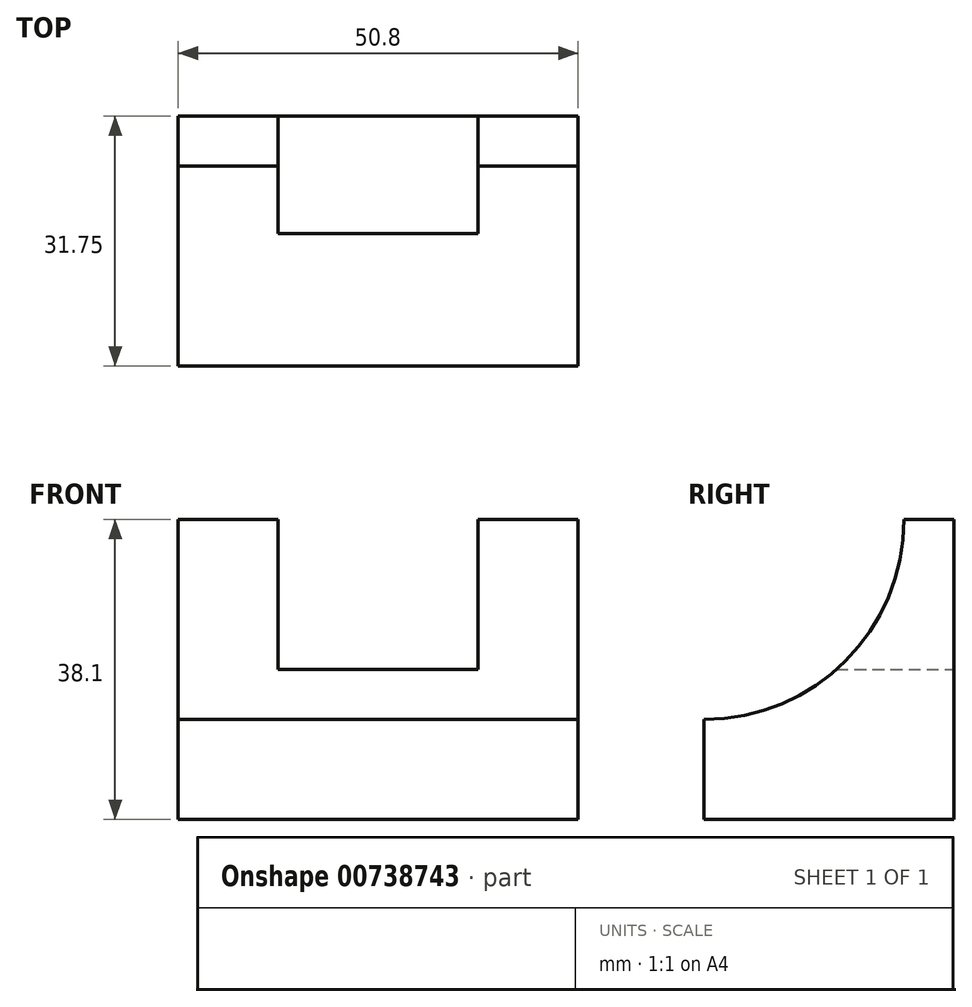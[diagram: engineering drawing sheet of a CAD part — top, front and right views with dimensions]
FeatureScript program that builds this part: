
annotation { "Feature Type Name" : "Feature", "Feature Type Description" : "" }
export const myFeature = defineFeature(function(context is Context, id is Id, definition is map)
    precondition{}
    {
        {
            var Q0;
            Q0=qCreatedBy(makeId("Right.planeOp"),FACE);
            var sketch = newSketch(context, id + "F0", { "sketchPlane" : qUnion([Q0])});
            skLineSegment(sketch, "E0", {"start": v(0, 0) * mm, "end": v(31.75, 0) * mm});
            skLineSegment(sketch, "E1", {"start": v(31.75, 0) * mm, "end": v(31.75, 38.1) * mm});
            skLineSegment(sketch, "E2", {"start": v(31.75, 38.1) * mm, "end": v(0, 38.1) * mm});
            skLineSegment(sketch, "E3", {"start": v(0, 38.1) * mm, "end": v(0, 0) * mm});
            skSolve(sketch);
        }
        {
            var Q0;
            Q0 = qSketchRegion(id + "F0", true);
            extrude(context, id + "F1", {"entities" : qUnion([Q0]), "depth" : 50.8 * mm, "offsetDistance" : 25.4 * mm});
        }
        {
            var Q0;
            Q0=makeQuery(id+"F1.opExtrude","CAP_FACE",FACE,{"disambiguationData":[OSD([sQuery(id+"F0.wireOp",EDGE,"E0"),sQuery(id+"F0.wireOp",EDGE,"E1"),sQuery(id+"F0.wireOp",EDGE,"E2"),sQuery(id+"F0.wireOp",EDGE,"E3")])],"isStart":true});
            var sketch = newSketch(context, id + "F2", { "sketchPlane" : qUnion([Q0])});
            skLineSegment(sketch, "E4", {"start": v(-31.75, 38.1) * mm, "end": v(-25.4, 38.1) * mm});
            skLineSegment(sketch, "E5", {"start": v(0, 0) * mm, "end": v(0, 12.7) * mm});
            skCircle(sketch, "E6", {"center": v(0, 38.1) * mm, "radius": 25.4 * mm});
            skSolve(sketch);
        }
        {
            var Q0;
            {var subQ1=makeQuery(id+"F1.opExtrude","CAP_EDGE",EDGE,{"disambiguationData":[OSD([sQuery(id+"F0.wireOp",EDGE,"E2")])],"isStart":true});var subQ3=makeQuery(id+"F1.opExtrude","CAP_EDGE",EDGE,{"disambiguationData":[OSD([sQuery(id+"F0.wireOp",EDGE,"E3")])],"isStart":true});var subQ5=makeQuery(id+"F2.imprint","INTERSECT",VERTEX,{"derivedFrom":[subQ1,subQ3]});Q0=makeQuery(id+"F2.imprint","IMPRINT",FACE,{"disambiguationData":[TD([[makeQuery(id+"F2.imprint","IMPRINT",EDGE,{"disambiguationData":[TD([[subQ5,1.0]])],"derivedFrom":subQ1}),-1.0]])]});}
            extrude(context, id + "F3", {"entities" : qUnion([Q0]), "operationType" : NewBodyOperationType.REMOVE, "endBound" : BoundingType.THROUGH_ALL, "oppositeDirection" : true, "depth" : 25.4 * mm, "offsetDistance" : 25.4 * mm});
        }
        {
            var Q0;
            Q0=makeQuery(id+"F1.opExtrude","SWEPT_FACE",FACE,{"disambiguationData":[OSD([sQuery(id+"F0.wireOp",EDGE,"E1")])]});
            var sketch = newSketch(context, id + "F4", { "sketchPlane" : qUnion([Q0])});
            skLineSegment(sketch, "E7", {"start": v(-38.1, 38.1) * mm, "end": v(-38.1, 19.05) * mm});
            skLineSegment(sketch, "E8", {"start": v(-38.1, 19.05) * mm, "end": v(-12.7, 19.05) * mm});
            skLineSegment(sketch, "E9", {"start": v(-12.7, 19.05) * mm, "end": v(-12.7, 38.1) * mm});
            skLineSegment(sketch, "E10", {"start": v(-12.7, 38.1) * mm, "end": v(-38.1, 38.1) * mm});
            skLineSegment(sketch, "E11", {"start": v(-38.1, 38.1) * mm, "end": v(-12.7, 38.1) * mm});
            skSolve(sketch);
        }
        {
            var Q0;
            Q0 = qSketchRegion(id + "F4", true);
            extrude(context, id + "F5", {"entities" : qUnion([Q0]), "operationType" : NewBodyOperationType.REMOVE, "oppositeDirection" : true, "depth" : 25.4 * mm, "offsetDistance" : 25.4 * mm});
        }
    });
